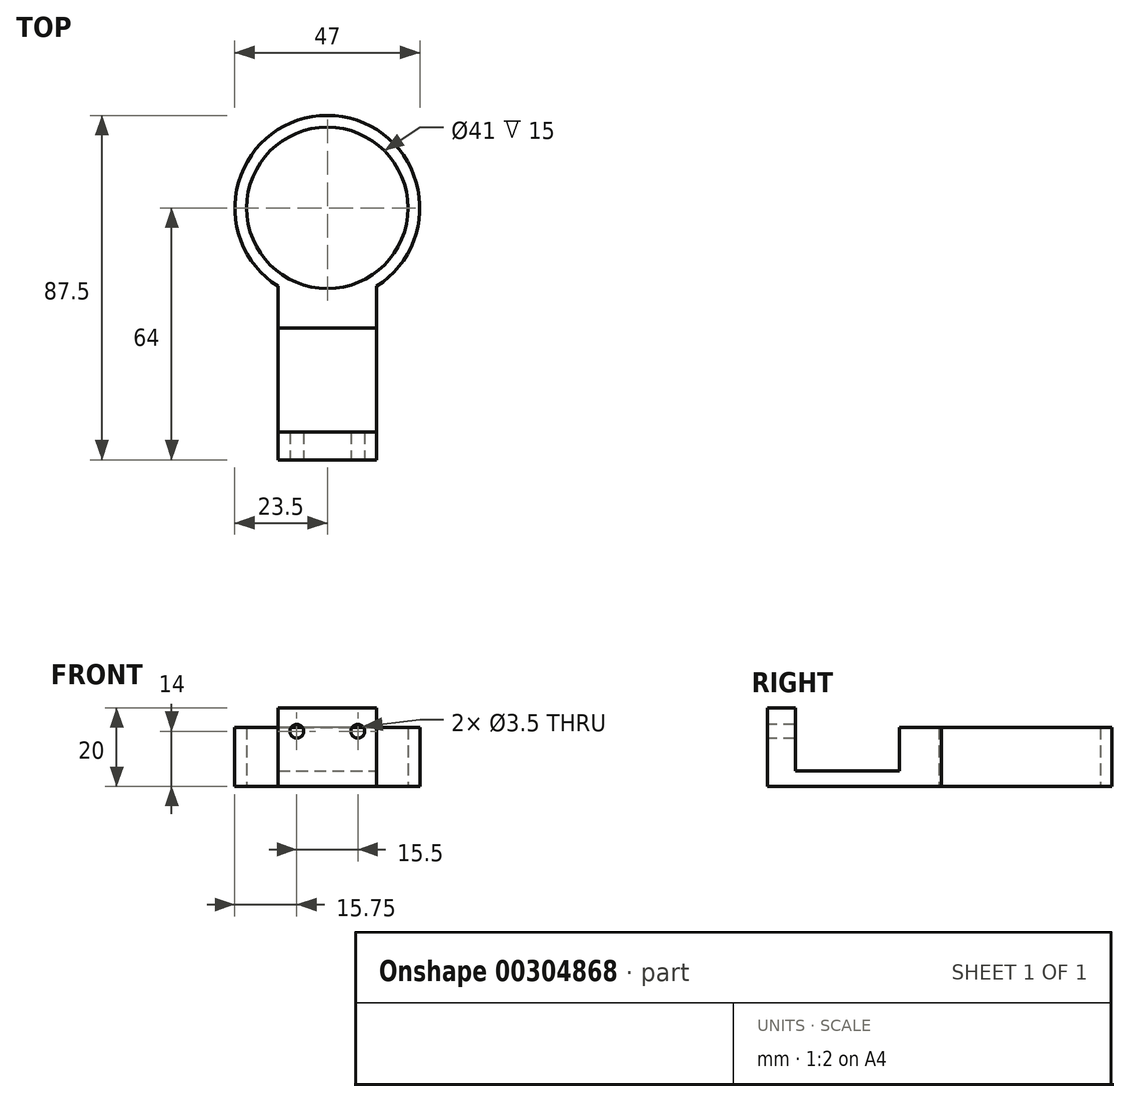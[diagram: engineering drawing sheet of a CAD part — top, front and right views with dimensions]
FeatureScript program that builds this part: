
annotation { "Feature Type Name" : "Feature", "Feature Type Description" : "" }
export const myFeature = defineFeature(function(context is Context, id is Id, definition is map)
    precondition{}
    {
        {
            var Q0;
            Q0=qCreatedBy(makeId("Top.planeOp"),FACE);
            var sketch = newSketch(context, id + "F0", { "sketchPlane" : qUnion([Q0])});
            skCircle(sketch, "E0", {"center": v(0, 0) * mm, "radius": 20.5 * mm});
            skLineSegment(sketch, "E1", {"start": v(-12.5, -19.9) * mm, "end": v(-12.5, -30.5) * mm});
            skLineSegment(sketch, "E2", {"start": v(-12.5, -30.5) * mm, "end": v(12.5, -30.5) * mm});
            skLineSegment(sketch, "E3", {"start": v(12.5, -19.9) * mm, "end": v(12.5, -30.5) * mm});
            skLineSegment(sketch, "E4.top", {"start": v(-12.5, -64) * mm, "end": v(12.5, -64) * mm});
            skLineSegment(sketch, "E4.left", {"start": v(-12.5, -30.5) * mm, "end": v(-12.5, -64) * mm});
            skLineSegment(sketch, "E4.right", {"start": v(12.5, -30.5) * mm, "end": v(12.5, -64) * mm});
            skLineSegment(sketch, "E5.left", {"start": v(-12.5, -64) * mm, "end": v(-12.5, -64) * mm});
            skLineSegment(sketch, "E5.right", {"start": v(12.5, -64) * mm, "end": v(12.5, -64) * mm});
            skLineSegment(sketch, "E6.top", {"start": v(-12.5, -57) * mm, "end": v(12.5, -57) * mm});
            skLineSegment(sketch, "E6.left", {"start": v(-12.5, -64) * mm, "end": v(-12.5, -57) * mm});
            skLineSegment(sketch, "E6.right", {"start": v(12.5, -64) * mm, "end": v(12.5, -57) * mm});
            skCircle(sketch, "E7.0", {"center": v(0, 0) * mm, "radius": 23.5 * mm});
            skLineSegment(sketch, "E8", {"start": v(0, 0) * mm, "end": v(0, -30.5) * mm, "construction": true});
            skSolve(sketch);
        }
        {
            var Q0;
            {var subQ0=sQuery(id+"F0.wireOp",EDGE,"E1");var subQ1=sQuery(id+"F0.wireOp",EDGE,"E0");var subQ2=makeQuery(id+"F0.imprint","INTERSECT",VERTEX,{"derivedFrom":[subQ1,subQ0]});Q0=makeQuery(id+"F0.imprint","IMPRINT",FACE,{"disambiguationData":[TD([[makeQuery(id+"F0.imprint","IMPRINT",EDGE,{"disambiguationData":[TD([[subQ2,1.0]])],"derivedFrom":subQ1}),-1.0]])]});}
            var Q1;
            {var subQ0=sQuery(id+"F0.wireOp",EDGE,"E1");var subQ1=sQuery(id+"F0.wireOp",EDGE,"E0");var subQ2=makeQuery(id+"F0.imprint","INTERSECT",VERTEX,{"derivedFrom":[subQ1,subQ0]});Q1=makeQuery(id+"F0.imprint","IMPRINT",FACE,{"disambiguationData":[TD([[makeQuery(id+"F0.imprint","IMPRINT",EDGE,{"disambiguationData":[TD([[subQ2,-1.0]])],"derivedFrom":subQ1}),-1.0]])]});}
            var Q2;
            {var subQ0=sQuery(id+"F0.wireOp",EDGE,"E2");Q2=makeQuery(id+"F0.imprint","IMPRINT",FACE,{"disambiguationData":[TD([[makeQuery(id+"F0.imprint","IMPRINT",EDGE,{"derivedFrom":subQ0}),1.0]])]});}
            extrude(context, id + "F1", {"entities" : qUnion([Q0, Q1, Q2]), "depth" : 15 * mm});
        }
        {
            var Q0;
            {var subQ0=sQuery(id+"F0.wireOp",EDGE,"E2");Q0=makeQuery(id+"F0.imprint","IMPRINT",FACE,{"disambiguationData":[TD([[makeQuery(id+"F0.imprint","IMPRINT",EDGE,{"derivedFrom":subQ0}),1.0]])]});}
            var Q1;
            Q1=makeQuery(id+"F0.imprint","IMPRINT",FACE,{"disambiguationData":[TD([[makeQuery(id+"F0.imprint","IMPRINT",EDGE,{"derivedFrom":sQuery(id+"F0.wireOp",EDGE,"E2")}),-1.0]])]});
            extrude(context, id + "F2", {"entities" : qUnion([Q0, Q1]), "operationType" : NewBodyOperationType.ADD, "depth" : 4 * mm});
        }
        {
            var Q0;
            Q0=makeQuery(id+"F0.imprint","IMPRINT",FACE,{"disambiguationData":[TD([[makeQuery(id+"F0.imprint","IMPRINT",EDGE,{"derivedFrom":sQuery(id+"F0.wireOp",EDGE,"E4.top")}),1.0]])]});
            extrude(context, id + "F3", {"entities" : qUnion([Q0]), "operationType" : NewBodyOperationType.ADD, "depth" : 20 * mm});
        }
        {
            var Q0;
            Q0=makeQuery(id+"F3.opExtrude","SWEPT_FACE",FACE,{"disambiguationData":[OSD([sQuery(id+"F0.wireOp",EDGE,"E4.top")])]});
            var sketch = newSketch(context, id + "F4", { "sketchPlane" : qUnion([Q0])});
            skLineSegment(sketch, "E9.0.0", {"start": v(-12.5, 0) * mm, "end": v(12.5, 0) * mm, "construction": true});
            skLineSegment(sketch, "E9.0.1", {"start": v(12.5, 0) * mm, "end": v(12.5, 20) * mm, "construction": true});
            skLineSegment(sketch, "E9.0.2", {"start": v(12.5, 20) * mm, "end": v(-12.5, 20) * mm, "construction": true});
            skLineSegment(sketch, "E9.0.3", {"start": v(-12.5, 20) * mm, "end": v(-12.5, 0) * mm, "construction": true});
            skLineSegment(sketch, "E10", {"start": v(0, 20) * mm, "end": v(0, 0) * mm, "construction": true});
            skCircle(sketch, "E11", {"center": v(-7.75, 14) * mm, "radius": 1.75 * mm});
            skCircle(sketch, "E12.MirrorC", {"center": v(7.75, 14) * mm, "radius": 1.75 * mm});
            skSolve(sketch);
        }
        {
            var Q0;
            Q0 = qSketchRegion(id + "F4", true);
            var Q1;
            Q1=makeQuery(id+"F3.opExtrude","SWEPT_FACE",FACE,{"disambiguationData":[OSD([sQuery(id+"F0.wireOp",EDGE,"E6.top")])]});
            extrude(context, id + "F5", {"entities" : qUnion([Q0]), "operationType" : NewBodyOperationType.REMOVE, "endBound" : BoundingType.UP_TO_SURFACE, "oppositeDirection" : true, "endBoundEntityFace" : qUnion([Q1]), "depth" : 25 * mm});
        }
    });
